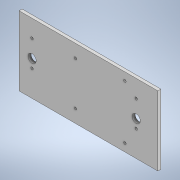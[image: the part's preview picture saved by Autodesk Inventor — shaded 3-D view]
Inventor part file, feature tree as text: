
AUTODESK INVENTOR PART (.ipt)
format: ipt  version: 2021 (Build 250183000, 183)  size: 165,888 bytes
history: native  units: mm
features: extrude x3, sketch x3
ambient origin geometry x8: Origin, YZ Plane, XZ Plane, XY Plane, X Axis, Y Axis, Z Axis, Center Point
bodies: Body1 (feature_tree)
feature tree (6):
  extrude  "Extrusion1"  Depth=110.0mm
  extrude  "Extrusion2"  Depth=80.0mm
  extrude  "Extrusion3"  Depth=10.0mm
  sketch  "Sketch2"  dims[d1=44.721mm d2=110.0mm]
  sketch  "Sketch3"  dims[d3=80.0mm d4=2.9mm]
  sketch  "Sketch4"  dims[d5=2.9mm d6=2.9mm d7=2.9mm d8=25.0mm d9=10.103mm d11=19.897mm d12=2.9mm d13=2.9mm d17=3.5mm d18=0.0mm d19=2.9mm d20=2.9mm d21=20.0mm d22=10.0mm d23=30.0mm d25=2.9mm d26=2.9mm d28=10.0mm d29=0.0mm d31=9.534mm d32=10.0mm d33=0.0mm]
